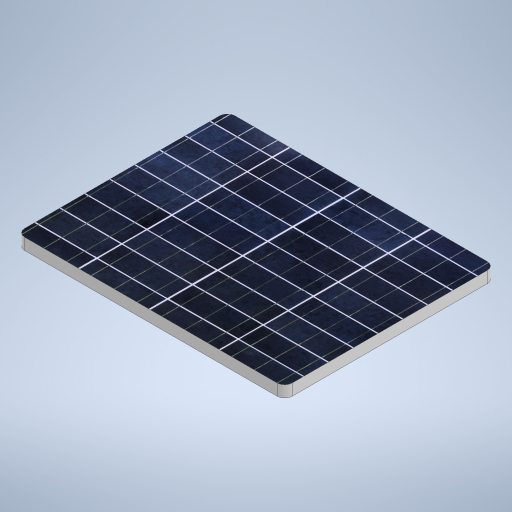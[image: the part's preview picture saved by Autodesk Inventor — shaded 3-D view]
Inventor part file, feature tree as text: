
AUTODESK INVENTOR PART (.ipt)
format: ipt  version: 2023 (Build 270158000, 158)  size: 488,448 bytes
history: native  units: mm
features: other x2, sketch x2, extrude x1, fillet x1
ambient origin geometry x8: Origin, YZ Plane, XZ Plane, XY Plane, X Axis, Y Axis, Z Axis, Center Point
bodies: Solid1 (feature_tree)
feature tree (6):
  extrude  "Extrusion1"  Depth=55.0mm
  fillet  "Fillet1"  Radius=3.0mm
  other  "Decal1"
  sketch  "Sketch1"  dims[d0=70.0mm d1=55.0mm d2=3.0mm d3=0.0mm]
  sketch  "Sketch2"  dims[d4=2.0mm d20=10.0mm d21=15.0mm d31=90.0mm d5=0.0mm d6=0.0mm d7=0.0mm]
  other  "Image1"
